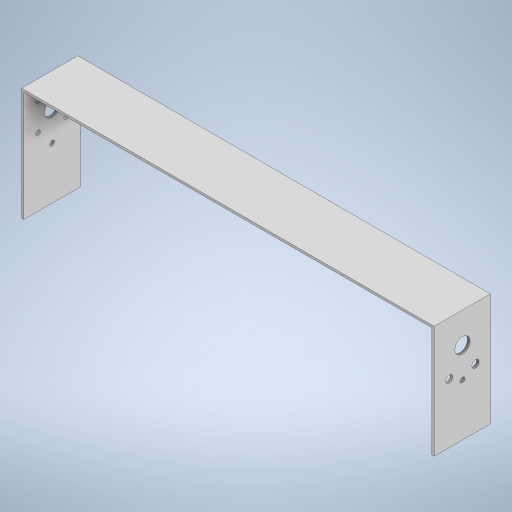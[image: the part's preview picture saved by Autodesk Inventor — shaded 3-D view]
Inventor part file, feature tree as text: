
AUTODESK INVENTOR PART (.ipt)
format: ipt  version: 2024 (Build 280153000, 153)  size: 262,656 bytes
history: native  units: in
note: dims shown in document units (in); Inventor stores cm internally (conversion verified against a paired STEP export)
features: extrude x5, sketch x5
ambient origin geometry x8: Origin, YZ Plane, XZ Plane, XY Plane, X Axis, Y Axis, Z Axis, Center Point
bodies: Solid1 (feature_tree)
feature tree (10):
  extrude  "Extrusion1"  Depth=3.0in
  extrude  "Extrusion2"  Depth=0.0625in
  extrude  "Extrusion3"  Depth=0.0625in
  extrude  "Extrusion4"  Depth=1.5in
  extrude  "Extrusion5"  TaperAngle=0.0deg  [1 undecoded]
  sketch  "Sketch1"  dims[d0=11.0in d1=3.0in]
  sketch  "Sketch2"  dims[d2=1.5in d3=0.0in d4=0.0625in]
  sketch  "Sketch3"  dims[d5=0.0625in d6=0.0625in]
  sketch  "Sketch4"  dims[d7=1.5in d8=0.0in d9=0.3976in]
  sketch  "Sketch5"  dims[d10=0.75in d11=0.0in d12=0.0in d13=0.125in d15=0.8in d16=0.4in d17=0.6in d18=0.1875in d19=1.0in d20=0.0in d21=0.125in d22=0.375in d23=0.375in d24=1.0in d25=0.0in]
note: 1 required parameter value undecoded (feature->parameter linkage not recoverable at this tier; creation-order binding heuristic only, values carry confidence <= 0.55)
